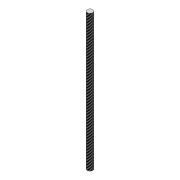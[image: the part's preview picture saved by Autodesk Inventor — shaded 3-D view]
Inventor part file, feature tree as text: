
AUTODESK INVENTOR PART (.ipt)
format: ipt  version: 2017 (Build 210142000, 142)  size: 73,216 bytes
history: native  units: mm
features: extrude x1, sketch x1
ambient origin geometry x8: Origin, YZ Plane, XZ Plane, XY Plane, X Axis, Y Axis, Z Axis, Center Point
bodies: Solid1 (feature_tree)
feature tree (2):
  extrude  "Extrusion1"  Depth=200.0mm TaperAngle=0.0deg
  sketch  "Sketch1"  dims[d0=8.0mm d1=200.0mm d2=0.0mm]
